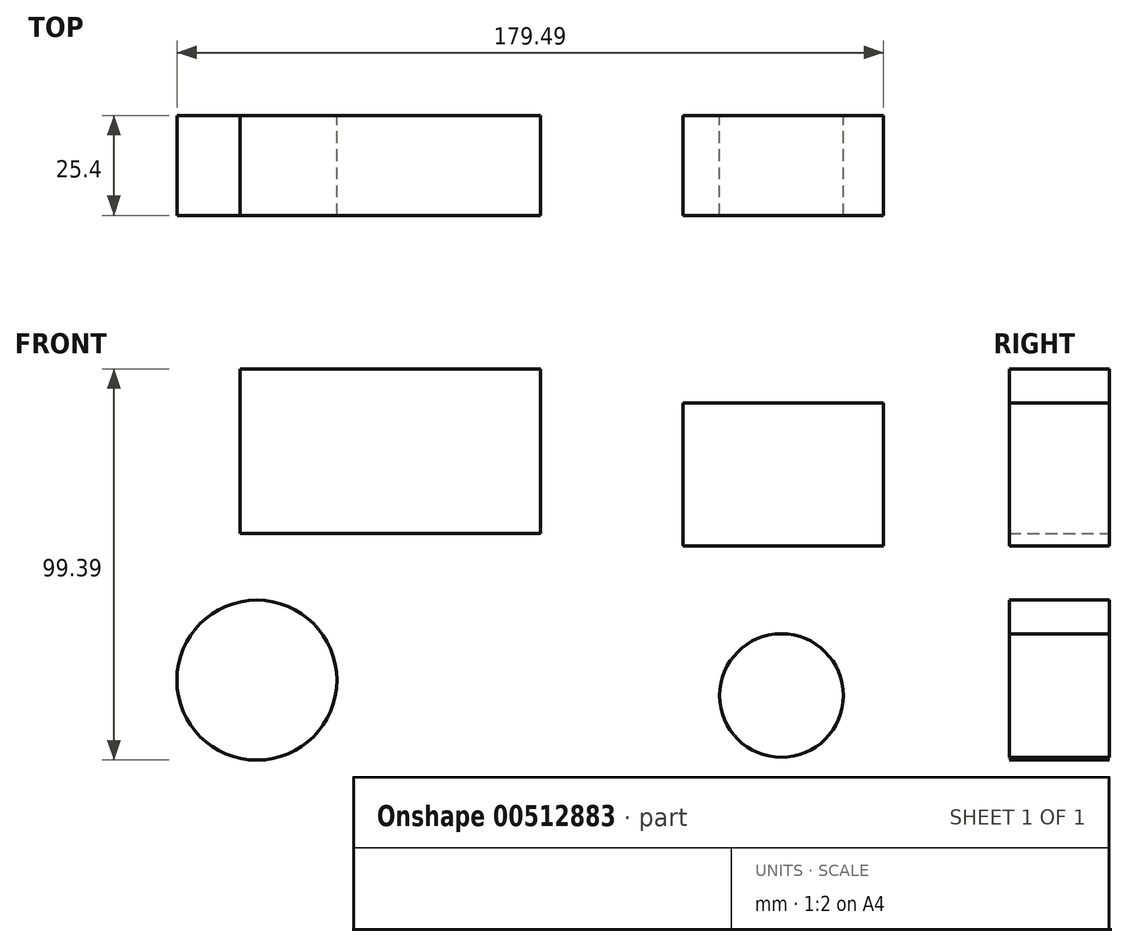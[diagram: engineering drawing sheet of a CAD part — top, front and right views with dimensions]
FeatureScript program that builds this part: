
annotation { "Feature Type Name" : "Feature", "Feature Type Description" : "" }
export const myFeature = defineFeature(function(context is Context, id is Id, definition is map)
    precondition{}
    {
        {
            var Q0;
            Q0=qCreatedBy(makeId("Front.planeOp"),FACE);
            var sketch = newSketch(context, id + "F0", { "sketchPlane" : qUnion([Q0])});
            skLineSegment(sketch, "E0.bottom", {"start": v(-72.26, 52.4) * mm, "end": v(4.09, 52.4) * mm});
            skLineSegment(sketch, "E0.top", {"start": v(-72.26, 10.65) * mm, "end": v(4.09, 10.65) * mm});
            skLineSegment(sketch, "E0.left", {"start": v(-72.26, 52.4) * mm, "end": v(-72.26, 10.65) * mm});
            skLineSegment(sketch, "E0.right", {"start": v(4.09, 52.4) * mm, "end": v(4.09, 10.65) * mm});
            skLineSegment(sketch, "E1.bottom", {"start": v(40.22, 43.71) * mm, "end": v(91.17, 43.71) * mm});
            skLineSegment(sketch, "E1.top", {"start": v(40.22, 7.41) * mm, "end": v(91.17, 7.41) * mm});
            skLineSegment(sketch, "E1.left", {"start": v(40.22, 43.71) * mm, "end": v(40.22, 7.41) * mm});
            skLineSegment(sketch, "E1.right", {"start": v(91.17, 43.71) * mm, "end": v(91.17, 7.41) * mm});
            skCircle(sketch, "E2", {"center": v(-68, -26.67) * mm, "radius": 20.32 * mm});
            skCircle(sketch, "E3", {"center": v(65.27, -30.59) * mm, "radius": 15.7 * mm});
            skSolve(sketch);
        }
        {
            var Q0;
            Q0 = qSketchRegion(id + "F0", true);
            extrude(context, id + "F1", {"entities" : qUnion([Q0]), "depth" : 25.4 * mm});
        }
    });
